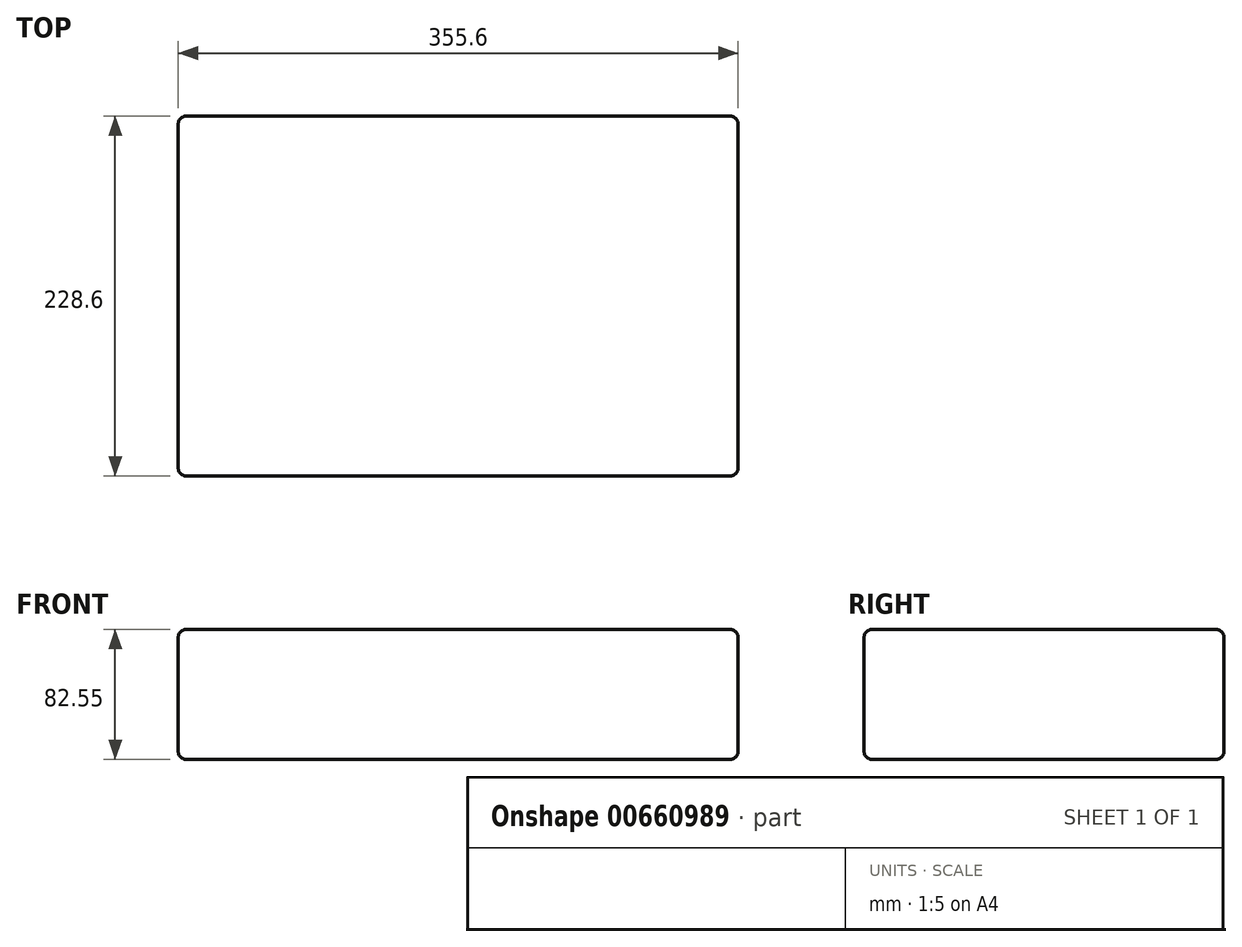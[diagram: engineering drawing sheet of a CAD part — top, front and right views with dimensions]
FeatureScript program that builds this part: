
annotation { "Feature Type Name" : "Feature", "Feature Type Description" : "" }
export const myFeature = defineFeature(function(context is Context, id is Id, definition is map)
    precondition{}
    {
        {
            var Q0;
            Q0=qCreatedBy(makeId("Top.planeOp"),FACE);
            var sketch = newSketch(context, id + "F0", { "sketchPlane" : qUnion([Q0])});
            skLineSegment(sketch, "E0.bottom", {"start": v(-311.7, 189.98) * mm, "end": v(43.9, 189.98) * mm});
            skLineSegment(sketch, "E0.top", {"start": v(-311.7, -38.62) * mm, "end": v(43.9, -38.62) * mm});
            skLineSegment(sketch, "E0.left", {"start": v(-311.7, 189.98) * mm, "end": v(-311.7, -38.62) * mm});
            skLineSegment(sketch, "E0.right", {"start": v(43.9, 189.98) * mm, "end": v(43.9, -38.62) * mm});
            skSolve(sketch);
        }
        {
            var Q0;
            Q0=makeQuery(id+"F0.imprint","IMPRINT",FACE,{"disambiguationData":[TD([[makeQuery(id+"F0.imprint","IMPRINT",EDGE,{"derivedFrom":sQuery(id+"F0.wireOp",EDGE,"E0.bottom")}),-1.0]])]});
            extrude(context, id + "F1", {"entities" : qUnion([Q0]), "depth" : 82.55 * mm, "offsetDistance" : 25.4 * mm});
        }
        {
            var Q0;
            Q0=makeQuery(id+"F1.opExtrude","CAP_EDGE",EDGE,{"disambiguationData":[OSD([sQuery(id+"F0.wireOp",EDGE,"E0.top")])],"isStart":false});
            var Q1;
            Q1=makeQuery(id+"F1.opExtrude","CAP_EDGE",EDGE,{"disambiguationData":[OSD([sQuery(id+"F0.wireOp",EDGE,"E0.right")])],"isStart":false});
            var Q2;
            Q2=makeQuery(id+"F1.opExtrude","CAP_EDGE",EDGE,{"disambiguationData":[OSD([sQuery(id+"F0.wireOp",EDGE,"E0.bottom")])],"isStart":false});
            var Q3;
            Q3=makeQuery(id+"F1.opExtrude","CAP_EDGE",EDGE,{"disambiguationData":[OSD([sQuery(id+"F0.wireOp",EDGE,"E0.left")])],"isStart":false});
            var Q4;
            Q4=makeQuery(id+"F1.opExtrude","CAP_EDGE",EDGE,{"disambiguationData":[OSD([sQuery(id+"F0.wireOp",EDGE,"E0.top")])],"isStart":true});
            var Q5;
            Q5=makeQuery(id+"F1.opExtrude","SWEPT_EDGE",EDGE,{"disambiguationData":[OSD([sQuery(id+"F0.wireOp",EDGE,"E0.top"),sQuery(id+"F0.wireOp",EDGE,"E0.left")])]});
            var Q6;
            Q6=makeQuery(id+"F1.opExtrude","SWEPT_EDGE",EDGE,{"disambiguationData":[OSD([sQuery(id+"F0.wireOp",EDGE,"E0.top"),sQuery(id+"F0.wireOp",EDGE,"E0.right")])]});
            var Q7;
            Q7=makeQuery(id+"F1.opExtrude","CAP_EDGE",EDGE,{"disambiguationData":[OSD([sQuery(id+"F0.wireOp",EDGE,"E0.right")])],"isStart":true});
            var Q8;
            Q8=makeQuery(id+"F1.opExtrude","CAP_EDGE",EDGE,{"disambiguationData":[OSD([sQuery(id+"F0.wireOp",EDGE,"E0.left")])],"isStart":true});
            var Q9;
            Q9=makeQuery(id+"F1.opExtrude","SWEPT_EDGE",EDGE,{"disambiguationData":[OSD([sQuery(id+"F0.wireOp",EDGE,"E0.bottom"),sQuery(id+"F0.wireOp",EDGE,"E0.left")])]});
            var Q10;
            Q10=makeQuery(id+"F1.opExtrude","CAP_EDGE",EDGE,{"disambiguationData":[OSD([sQuery(id+"F0.wireOp",EDGE,"E0.bottom")])],"isStart":true});
            var Q11;
            Q11=makeQuery(id+"F1.opExtrude","SWEPT_EDGE",EDGE,{"disambiguationData":[OSD([sQuery(id+"F0.wireOp",EDGE,"E0.bottom"),sQuery(id+"F0.wireOp",EDGE,"E0.right")])]});
            fillet(context, id + "F2", {"entities" : qUnion([Q0, Q1, Q2, Q3, Q4, Q5, Q6, Q7, Q8, Q9, Q10, Q11]), "radius" : 5.08 * mm, "tangentPropagation" : true, "allowEdgeOverflow" : false});
        }
    });
